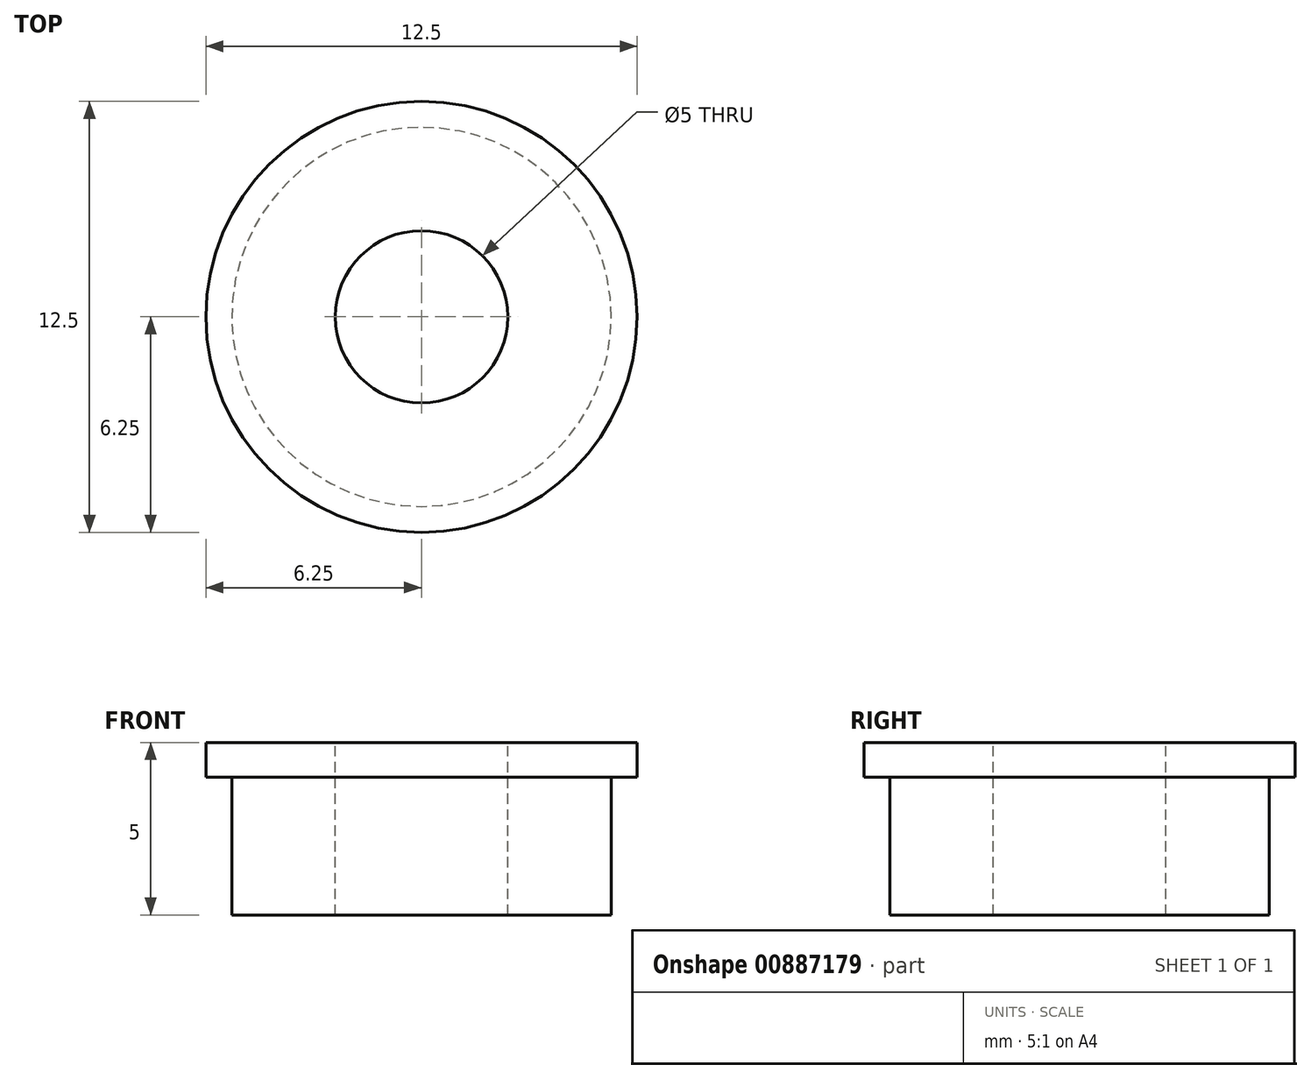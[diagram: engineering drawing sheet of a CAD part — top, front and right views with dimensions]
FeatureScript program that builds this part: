
annotation { "Feature Type Name" : "Feature", "Feature Type Description" : "" }
export const myFeature = defineFeature(function(context is Context, id is Id, definition is map)
    precondition{}
    {
        {
            var Q0;
            Q0=qCreatedBy(makeId("Right.planeOp"),FACE);
            var sketch = newSketch(context, id + "F0", { "sketchPlane" : qUnion([Q0])});
            skLineSegment(sketch, "E0.bottom", {"start": v(-5.5, 0) * mm, "end": v(-2.5, 0) * mm, "construction": true});
            skLineSegment(sketch, "E0.left", {"start": v(-5.5, 0) * mm, "end": v(-5.5, 4) * mm, "construction": true});
            skLineSegment(sketch, "E0.right", {"start": v(5.5, 0) * mm, "end": v(5.5, 4) * mm});
            skLineSegment(sketch, "E1.bottom", {"start": v(-6.25, 5) * mm, "end": v(-2.5, 5) * mm, "construction": true});
            skLineSegment(sketch, "E1.top", {"start": v(-6.25, 4) * mm, "end": v(-5.5, 4) * mm, "construction": true});
            skLineSegment(sketch, "E1.left", {"start": v(-6.25, 5) * mm, "end": v(-6.25, 4) * mm, "construction": true});
            skLineSegment(sketch, "E1.right", {"start": v(6.25, 5) * mm, "end": v(6.25, 4) * mm});
            skLineSegment(sketch, "E2", {"start": v(-2.5, 5) * mm, "end": v(-2.5, 0) * mm, "construction": true});
            skLineSegment(sketch, "E3.MirrorCS", {"start": v(2.5, 5) * mm, "end": v(2.5, 0) * mm});
            skLineSegment(sketch, "E4.trimOffspring", {"start": v(2.5, 5) * mm, "end": v(6.25, 5) * mm});
            skLineSegment(sketch, "E5.trimOffspring", {"start": v(5.5, 4) * mm, "end": v(6.25, 4) * mm});
            skLineSegment(sketch, "E6.trimOffspring", {"start": v(2.5, 0) * mm, "end": v(5.5, 0) * mm});
            skLineSegment(sketch, "E7", {"start": v(0, 6.62) * mm, "end": v(0, -4.14) * mm, "construction": true});
            skSolve(sketch);
        }
        {
            var Q0;
            Q0=qSketchRegion(id+"F0",true);
            var Q1;
            Q1=sQuery(id+"F0.wireOp",EDGE,"E7");
            revolve(context, id + "F1", {"surfaceOperationType" : NewSurfaceOperationType.NEW, "entities" : qUnion([Q0]), "axis" : qUnion([Q1]), "revolveType" : RevolveType.FULL});
        }
    });
